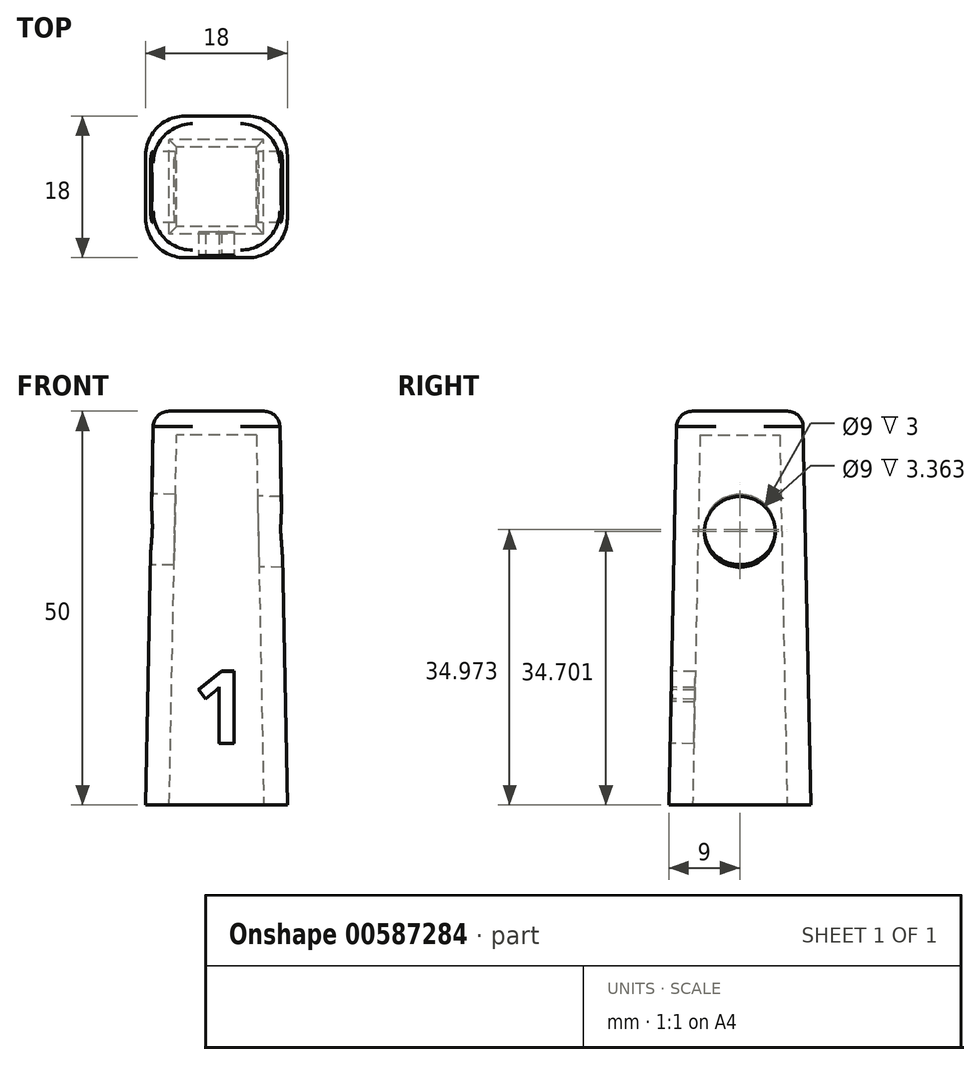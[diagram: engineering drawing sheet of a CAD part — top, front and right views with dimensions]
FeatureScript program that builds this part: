
annotation { "Feature Type Name" : "Feature", "Feature Type Description" : "" }
export const myFeature = defineFeature(function(context is Context, id is Id, definition is map)
    precondition{}
    {
        {
            var Q0;
            Q0=qCreatedBy(makeId("Top.planeOp"),FACE);
            cPlane(context, id + "F0", {"entities" : qUnion([Q0]), "cplaneType" : CPlaneType.OFFSET, "offset" : 50 * mm, "width" : 150 * mm, "height" : 150 * mm});
        }
        {
            var Q0;
            Q0=qCreatedBy(makeId("Top.planeOp"),FACE);
            var sketch = newSketch(context, id + "F1", { "sketchPlane" : qUnion([Q0])});
            skLineSegment(sketch, "E0.bottom", {"start": v(9, -9) * mm, "end": v(-9, -9) * mm});
            skLineSegment(sketch, "E0.top", {"start": v(9, 9) * mm, "end": v(-9, 9) * mm});
            skLineSegment(sketch, "E0.left", {"start": v(9, -9) * mm, "end": v(9, 9) * mm});
            skLineSegment(sketch, "E0.right", {"start": v(-9, -9) * mm, "end": v(-9, 9) * mm});
            skPoint(sketch, "E0.middle", {"position": v(0, 0) * mm});
            skSolve(sketch);
        }
        {
            var Q0;
            Q0=qCreatedBy(id+"F0.planeOp",FACE);
            var sketch = newSketch(context, id + "F2", { "sketchPlane" : qUnion([Q0])});
            skLineSegment(sketch, "E1.bottom", {"start": v(8, -8) * mm, "end": v(-8, -8) * mm});
            skLineSegment(sketch, "E1.top", {"start": v(8, 8) * mm, "end": v(-8, 8) * mm});
            skLineSegment(sketch, "E1.left", {"start": v(8, -8) * mm, "end": v(8, 8) * mm});
            skLineSegment(sketch, "E1.right", {"start": v(-8, -8) * mm, "end": v(-8, 8) * mm});
            skPoint(sketch, "E1.middle", {"position": v(0, 0) * mm});
            skSolve(sketch);
        }
        {
            var Q0;
            Q0=makeQuery(id+"F1.imprint","IMPRINT",FACE,{"disambiguationData":[TD([[makeQuery(id+"F1.imprint","IMPRINT",EDGE,{"derivedFrom":sQuery(id+"F1.wireOp",EDGE,"E0.bottom")}),-1.0]])]});
            var Q1;
            Q1=makeQuery(id+"F2.imprint","IMPRINT",FACE,{"disambiguationData":[TD([[makeQuery(id+"F2.imprint","IMPRINT",EDGE,{"derivedFrom":sQuery(id+"F2.wireOp",EDGE,"E1.bottom")}),-1.0]])]});
            loft(context, id + "F3", {"sheetProfilesArray" : [{ "sheetProfileEntities" : qUnion([Q0]) }, { "sheetProfileEntities" : qUnion([Q1]) }]});
        }
        {
            var Q0;
            Q0=makeQuery(id+"F3.opLoft","CAP_FACE",FACE,{"disambiguationData":[OSD([makeQuery(id+"F1.imprint","IMPRINT",FACE,{"disambiguationData":[TD([[makeQuery(id+"F1.imprint","IMPRINT",EDGE,{"derivedFrom":sQuery(id+"F1.wireOp",EDGE,"E0.bottom")}),-1.0]])]})])],"isStart":true});
            shell(context, id + "F4", {"entities" : qUnion([Q0]), "thickness" : 3 * mm});
        }
        {
            var Q0;
            Q0=makeQuery(id+"F3.opLoft","SWEPT_FACE",FACE,{"disambiguationData":[OSD([sQuery(id+"F1.wireOp",EDGE,"E0.bottom"),sQuery(id+"F1.wireOp",EDGE,"E0.left"),sQuery(id+"F1.wireOp",EDGE,"E0.right"),sQuery(id+"F2.wireOp",EDGE,"E1.bottom"),sQuery(id+"F2.wireOp",EDGE,"E1.left"),sQuery(id+"F2.wireOp",EDGE,"E1.right")])]});
            var sketch = newSketch(context, id + "F5", { "sketchPlane" : qUnion([Q0])});
            skLineSegment(sketch, "E2", {"start": v(0, 49.83) * mm, "end": v(0, 0) * mm, "construction": true});
            skText(sketch, "E3", { "text": "1", "fontName": "OpenSans-Bold.ttf"});
            const initialGuessF5  = {"E3": [-0.00307, 0.00764, 1, 0, 0.00925]};
            skSetInitialGuess(sketch, initialGuessF5);
            skSolve(sketch);
        }
        {
            var Q0;
            Q0=makeQuery(id+"F5.imprint","IMPRINT",FACE,{"disambiguationData":[TD([[makeQuery(id+"F5.imprint","IMPRINT",EDGE,{"derivedFrom":sQuery(id+"F5.wireOp",EDGE,"E3.sketch_text.stroke-0")}),-1.0]])]});
            extrude(context, id + "F6", {"entities" : qUnion([Q0]), "operationType" : NewBodyOperationType.REMOVE, "endBound" : BoundingType.UP_TO_NEXT, "oppositeDirection" : true, "depth" : 25 * mm, "offsetDistance" : 25 * mm});
        }
        {
            var Q0;
            Q0=makeQuery(id+"F3.opLoft","SWEPT_FACE",FACE,{"disambiguationData":[OSD([sQuery(id+"F1.wireOp",EDGE,"E0.bottom"),sQuery(id+"F1.wireOp",EDGE,"E0.top"),sQuery(id+"F1.wireOp",EDGE,"E0.right"),sQuery(id+"F2.wireOp",EDGE,"E1.bottom"),sQuery(id+"F2.wireOp",EDGE,"E1.top"),sQuery(id+"F2.wireOp",EDGE,"E1.right")])]});
            var sketch = newSketch(context, id + "F7", { "sketchPlane" : qUnion([Q0])});
            skLineSegment(sketch, "E4", {"start": v(0, 53.8) * mm, "end": v(0, -5.02) * mm, "construction": true});
            skPoint(sketch, "E4.startSnap0", {"position": v(0, 49.83) * mm});
            skCircle(sketch, "E5", {"center": v(0, 34.83) * mm, "radius": 4.5 * mm});
            skSolve(sketch);
        }
        {
            var Q0;
            Q0=makeQuery(id+"F7.imprint","IMPRINT",FACE,{"disambiguationData":[TD([[makeQuery(id+"F7.imprint","IMPRINT",EDGE,{"derivedFrom":sQuery(id+"F7.wireOp",EDGE,"E5")}),1.0]])]});
            extrude(context, id + "F8", {"entities" : qUnion([Q0]), "operationType" : NewBodyOperationType.REMOVE, "endBound" : BoundingType.THROUGH_ALL, "oppositeDirection" : true, "depth" : 25 * mm, "offsetDistance" : 25 * mm});
        }
        {
            var Q0;
            Q0=makeQuery(id+"F3.opLoft","SWEPT_EDGE",EDGE,{"disambiguationData":[OSD([sQuery(id+"F1.wireOp",EDGE,"E0.bottom"),sQuery(id+"F1.wireOp",EDGE,"E0.left"),sQuery(id+"F2.wireOp",EDGE,"E1.bottom"),sQuery(id+"F2.wireOp",EDGE,"E1.left")])]});
            var Q1;
            Q1=makeQuery(id+"F3.opLoft","SWEPT_EDGE",EDGE,{"disambiguationData":[OSD([sQuery(id+"F1.wireOp",EDGE,"E0.top"),sQuery(id+"F1.wireOp",EDGE,"E0.left"),sQuery(id+"F2.wireOp",EDGE,"E1.top"),sQuery(id+"F2.wireOp",EDGE,"E1.left")])]});
            var Q2;
            Q2=makeQuery(id+"F3.opLoft","SWEPT_EDGE",EDGE,{"disambiguationData":[OSD([sQuery(id+"F1.wireOp",EDGE,"E0.top"),sQuery(id+"F1.wireOp",EDGE,"E0.right"),sQuery(id+"F2.wireOp",EDGE,"E1.top"),sQuery(id+"F2.wireOp",EDGE,"E1.right")])]});
            var Q3;
            Q3=makeQuery(id+"F3.opLoft","SWEPT_EDGE",EDGE,{"disambiguationData":[OSD([sQuery(id+"F1.wireOp",EDGE,"E0.bottom"),sQuery(id+"F1.wireOp",EDGE,"E0.right"),sQuery(id+"F2.wireOp",EDGE,"E1.bottom"),sQuery(id+"F2.wireOp",EDGE,"E1.right")])]});
            fillet(context, id + "F9", {"entities" : qUnion([Q0, Q1, Q2, Q3]), "radius" : 5 * mm, "tangentPropagation" : true, "allowEdgeOverflow" : false});
        }
        {
            var Q0;
            Q0=makeQuery(id+"F3.opLoft","CAP_FACE",FACE,{"disambiguationData":[OSD([makeQuery(id+"F2.imprint","IMPRINT",FACE,{"disambiguationData":[TD([[makeQuery(id+"F2.imprint","IMPRINT",EDGE,{"derivedFrom":sQuery(id+"F2.wireOp",EDGE,"E1.bottom")}),-1.0]])]})])],"isStart":true});
            fillet(context, id + "F10", {"entities" : qUnion([Q0]), "radius" : 2 * mm, "tangentPropagation" : true, "allowEdgeOverflow" : false});
        }
    });
